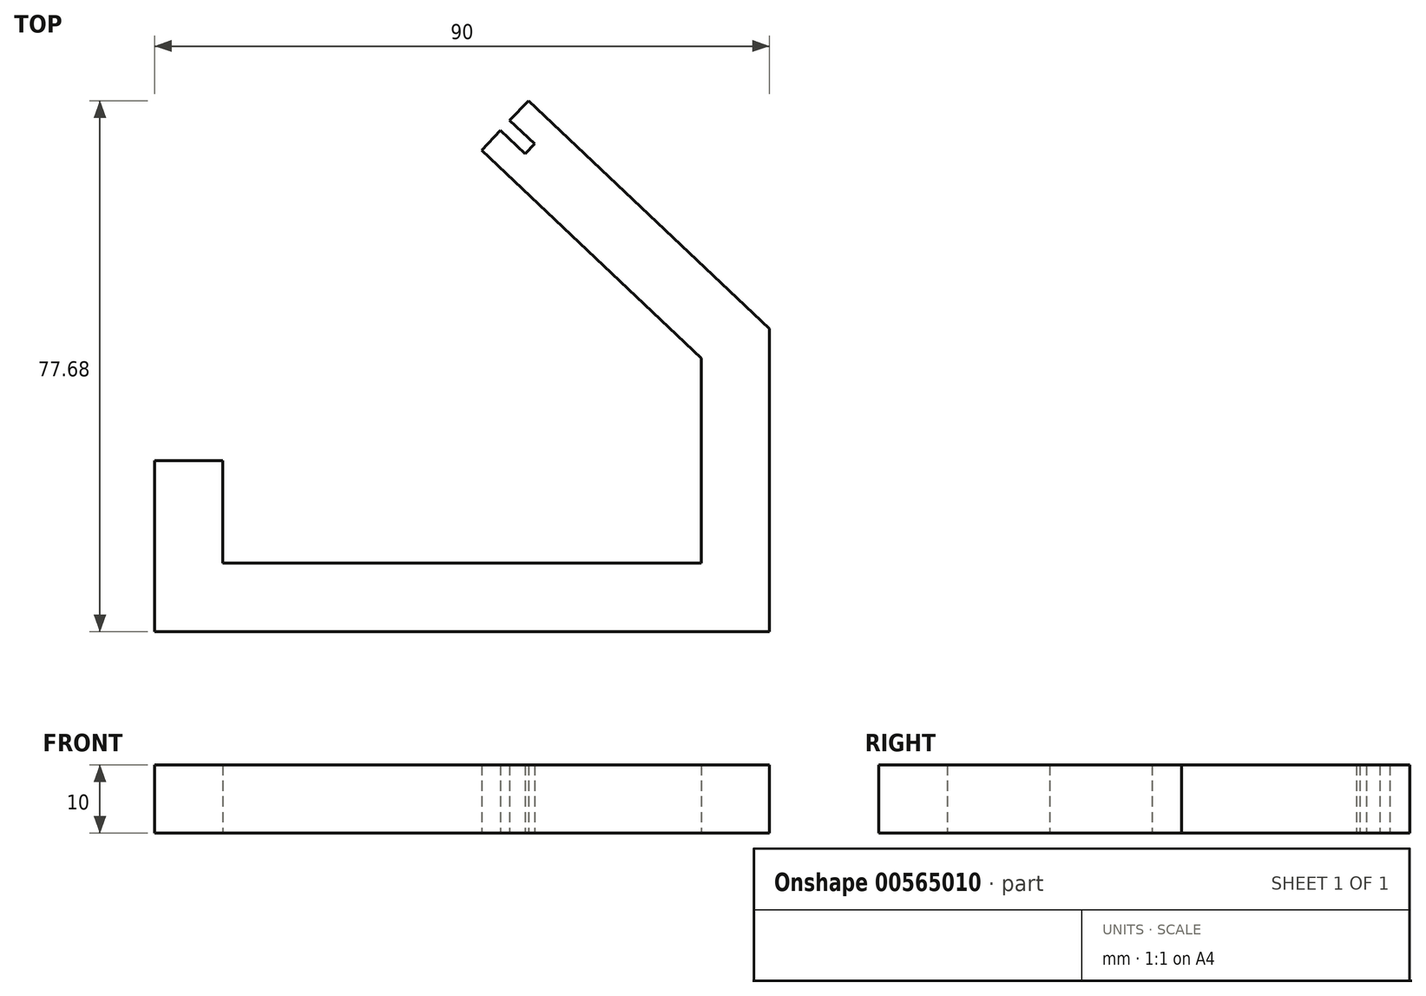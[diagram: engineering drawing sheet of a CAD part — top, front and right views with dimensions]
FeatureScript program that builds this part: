
annotation { "Feature Type Name" : "Feature", "Feature Type Description" : "" }
export const myFeature = defineFeature(function(context is Context, id is Id, definition is map)
    precondition{}
    {
        {
            var Q0;
            Q0=qCreatedBy(makeId("Top.planeOp"),FACE);
            var sketch = newSketch(context, id + "F0", { "sketchPlane" : qUnion([Q0])});
            skPoint(sketch, "E0", {"position": v(0, -40) * mm});
            skLineSegment(sketch, "E1", {"start": v(0, -40) * mm, "end": v(-45, -40) * mm});
            skLineSegment(sketch, "E2", {"start": v(-45, -40) * mm, "end": v(-45, -15) * mm});
            skLineSegment(sketch, "E3", {"start": v(35, -30) * mm, "end": v(35, 0) * mm});
            skLineSegment(sketch, "E4", {"start": v(0, -40) * mm, "end": v(45, -40) * mm});
            skLineSegment(sketch, "E5", {"start": v(45, -40) * mm, "end": v(45, 0) * mm});
            skLineSegment(sketch, "E6", {"start": v(-45, -15) * mm, "end": v(-35, -15) * mm});
            skLineSegment(sketch, "E7", {"start": v(-35, -15) * mm, "end": v(-35, -30) * mm});
            skLineSegment(sketch, "E8", {"start": v(-35, -30) * mm, "end": v(35, -30) * mm});
            skPoint(sketch, "E9", {"position": v(2.85, 30.42) * mm});
            skPoint(sketch, "E10", {"position": v(9.73, 37.68) * mm});
            skLineSegment(sketch, "E11", {"start": v(35, 0) * mm, "end": v(2.85, 30.42) * mm});
            skLineSegment(sketch, "E12", {"start": v(9.73, 37.68) * mm, "end": v(45, 4.3) * mm});
            skLineSegment(sketch, "E13", {"start": v(45, 0) * mm, "end": v(45, 4.3) * mm});
            skLineSegment(sketch, "E14", {"start": v(2.85, 30.42) * mm, "end": v(5.6, 33.32) * mm});
            skLineSegment(sketch, "E15", {"start": v(5.6, 33.32) * mm, "end": v(9.24, 29.89) * mm});
            skLineSegment(sketch, "E16", {"start": v(9.24, 29.89) * mm, "end": v(10.6, 31.34) * mm});
            skLineSegment(sketch, "E17", {"start": v(10.6, 31.34) * mm, "end": v(6.98, 34.77) * mm});
            skLineSegment(sketch, "E18", {"start": v(6.98, 34.77) * mm, "end": v(9.73, 37.68) * mm});
            skSolve(sketch);
        }
        {
            var Q0;
            Q0=makeQuery(id+"F0.imprint","IMPRINT",FACE,{"disambiguationData":[TD([[makeQuery(id+"F0.imprint","IMPRINT",EDGE,{"derivedFrom":sQuery(id+"F0.wireOp",EDGE,"E1")}),-1.0]])]});
            extrude(context, id + "F1", {"entities" : qUnion([Q0]), "depth" : 10 * mm, "offsetDistance" : 25 * mm});
        }
    });
